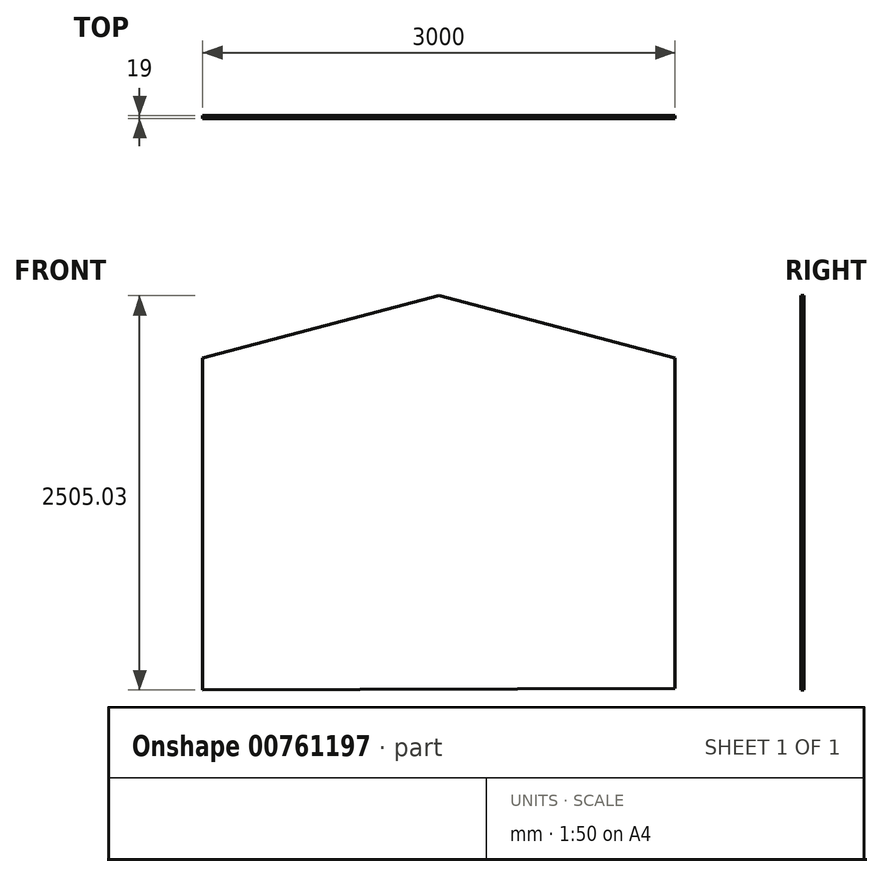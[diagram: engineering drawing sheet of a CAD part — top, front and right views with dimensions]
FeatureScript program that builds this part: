
annotation { "Feature Type Name" : "Feature", "Feature Type Description" : "" }
export const myFeature = defineFeature(function(context is Context, id is Id, definition is map)
    precondition{}
    {
        {
            var Q0;
            Q0=qCreatedBy(makeId("Front.planeOp"),FACE);
            var sketch = newSketch(context, id + "F0", { "sketchPlane" : qUnion([Q0])});
            skLineSegment(sketch, "E0.bottom", {"start": v(19, 5.05) * mm, "end": v(-2981, -4.97) * mm});
            skLineSegment(sketch, "E1", {"start": v(19, 2105.07) * mm, "end": v(-1481, 2500.06) * mm});
            skLineSegment(sketch, "E2", {"start": v(-1481, 2500.06) * mm, "end": v(-2981, 2105.07) * mm});
            skLineSegment(sketch, "E3", {"start": v(19, 2105.07) * mm, "end": v(19, 5.05) * mm});
            skLineSegment(sketch, "E4", {"start": v(-2981, 2105.07) * mm, "end": v(-2981, -4.97) * mm});
            skSolve(sketch);
        }
        {
            var Q0;
            Q0 = qSketchRegion(id + "F0", true);
            extrude(context, id + "F1", {"entities" : qUnion([Q0]), "depth" : 19 * mm, "offsetDistance" : 25 * mm});
        }
    });
